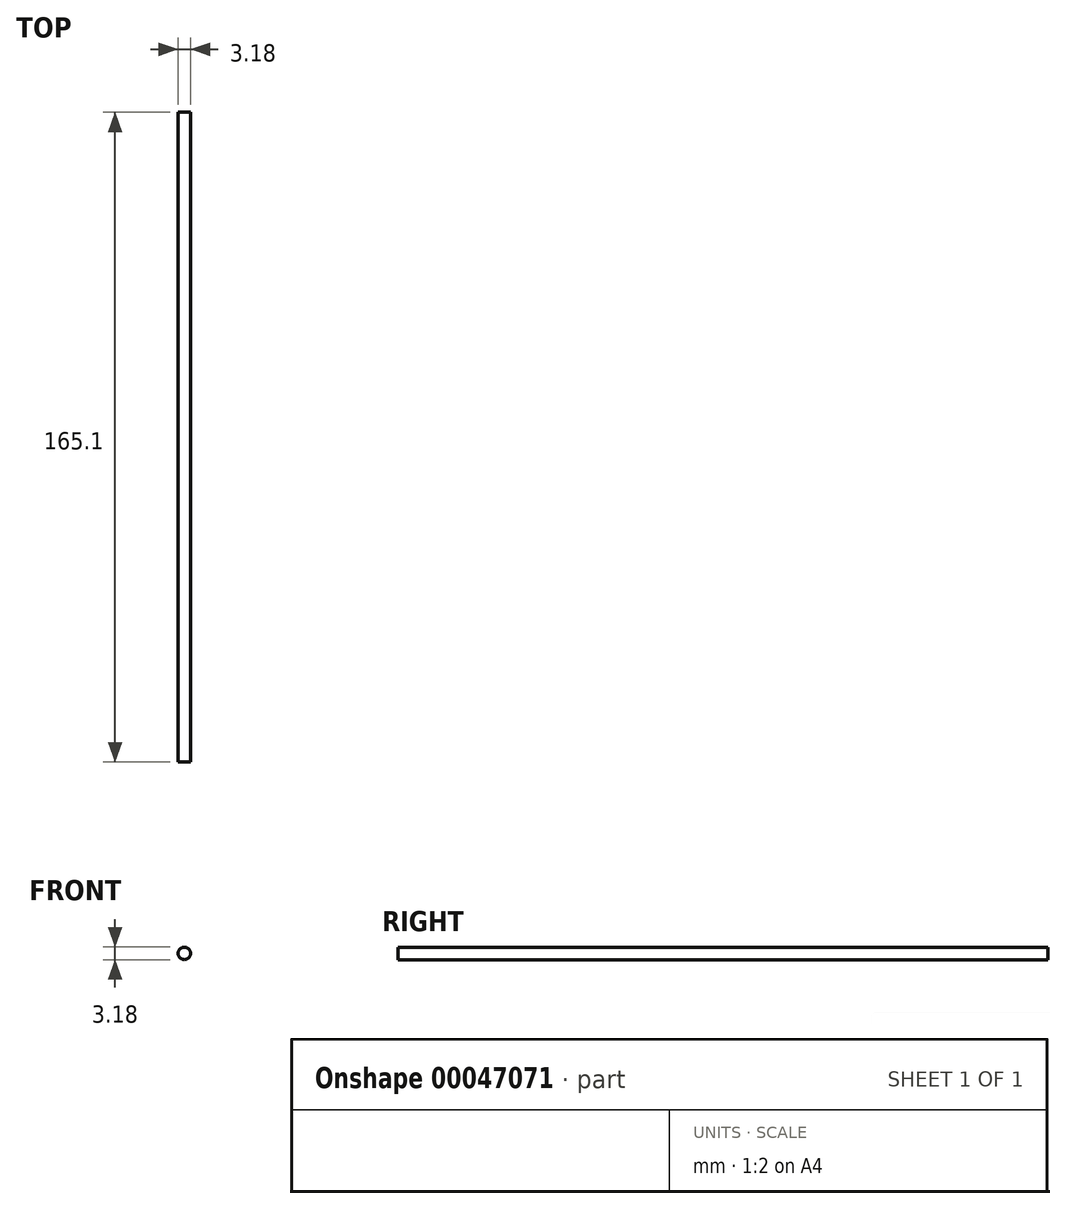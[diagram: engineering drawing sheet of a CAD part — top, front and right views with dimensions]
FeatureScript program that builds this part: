
annotation { "Feature Type Name" : "Feature", "Feature Type Description" : "" }
export const myFeature = defineFeature(function(context is Context, id is Id, definition is map)
    precondition{}
    {
        {
            var Q0;
            Q0=qCreatedBy(makeId("Front.planeOp"),FACE);
            var sketch = newSketch(context, id + "F0", { "sketchPlane" : qUnion([Q0])});
            skCircle(sketch, "E0", {"center": v(0, 0) * mm, "radius": 1.59 * mm});
            skSolve(sketch);
        }
        {
            var Q0;
            Q0=qSketchRegion(id+"F0",true);
            extrude(context, id + "F1", {"entities" : qUnion([Q0]), "endBound" : BoundingType.SYMMETRIC, "depth" : 165.1 * mm});
        }
    });
